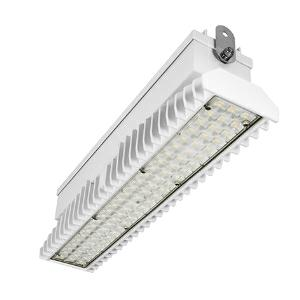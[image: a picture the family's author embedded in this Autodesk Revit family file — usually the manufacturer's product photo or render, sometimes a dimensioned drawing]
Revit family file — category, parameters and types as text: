
# Revit family: 3f_filippi_-_3f_lem_ho_ampio_3f_filippi_-_58953_a0811_-_3f_lem_1_ho_led_70_cr_ampio___vt_01d9
name_source: partatom
category: Lighting Fixtures
units: mm (PartAtom-declared; Revit-internal decimal feet)

## family parameters
Cut with Voids When Loaded = No
Host = Face
Light Source = No
Part Type = Normal
Room Calculation Point = No
Round Connector Dimension = Use Diameter
Shared = No

## types (1)
- 3F Filippi - 3F LEM HO Ampio (1 x LED, 10526 lm, 71 W, 4000 K)
    Apparent Load = 71 VA
    Approval mark = CE
    CIE Flux Codes = 60 92 99 100 100
    Color Rendering = 80
    Color Temperature = 4000 K
    Control Gear = Electronic ballast
    Default Elevation = 1800 mm
    Description = Industrial luminaire with high light output and high luminous efficiency designed with the most innovative technologies for environments with temperature up to 55°C.

ILLUMINOTECHNICAL
Luminous efficiency 100% (DLOR 99%, ULOR 1%).
Initial luminous flux of the luminaire 10526 lm.
Direct symmetric wide distribution: the illuminated area has a rectangular shape.
Installation Interdistance Transv.D = 1.58 x hu - Long.D = 1.45 x hu.
Tabular UGR (CIE 117 - 4H-8H; S=0.25H; 70/50/20): RUG 26.9 - 27.8.
Beam angle: 93° - 99°.
Luminous efficacy 148 lm/W.
Lifetime (L93/B10): 30000 h. (tq+25°C)
Lifetime (L90/B10): 50000 h. (tq+25°C)
Lifetime (L85/B10): 80000 h. (tq+25°C)
Lifetime (L80/B10): 100000 h. (tq+25°C)
Lifetime (L85/B10): 50000 h. (tq+55°C)
Sudden decreased luminous flux after 50000 hours: 0% (C0).
Photobiological safety in compliance with IEC/TR 62778: RG0 risk exempt, (IEC 62471).
In compliance with IEC/EN 62722-2-1 - IEC/EN 62717 standards.

SOURCE
Mid-Power linear LED module 70W/840.
Energy efficiency class (UE 2019/2020 - UE 2019/2015): C.
CIE 13.3 Colour rendering index: CRI >80 (R9 <50%).
IES TM-30 Fidelity Index: Rf = 84 Rg = 95.
CCT nominal colour temperature 4000 K.
Colour initial tolerance (MacAdam): SDCM 3.

MECHANICAL
Passive modular heatsinks in die-casted aluminium, painted in white colour.
To optimize the thermal management of the LED module, the heatsinks are oversized and provided with self-cleaning of cooling fins.
Wiring body in aluminium and galvanised steel anchored solidly to the sinks and thermally separated.
3F Lens lenses with high luminous efficiency, transparent methacrylate (PMMA), fixed to the LED modules.
Fixing brackets in stainless steel.
Luminaire with limited surface temperature. - D - (EN 60598-2-24)
Dimensions: 542x115 mm, height 154 mm. Weight 6.477 kg.
IP65 protection degree.
Mechanical strength to impacts IK06 (1 joule).
Glow-wire test resistance 650°C.

ELECTRICAL
Halogen Free electronic wiring 230V-50/60Hz, power factor 0.97, THD <25%, constant output current, class I, 1 driver.
Power of the luminaire 71 W.
ENEC - CE.
SAFE FLICKER: PstLM=<1 and SVM=<0.4 (IEC TR 61547-1 and IEC TR 63158), to ensure a more comfortable and safe light.
Luminaire compliant with EN 60598-2-22 for power supply from a centralised emergency system CPSS (Central Power Supply System), not incorporated in the luminaire - high risk areas excluded. The default power and flux are 100% in AC and 100% in DC.
Ambient temperature from -30°C to +55°C.
Temperature class T6 max 85°C.
Quick connection via M20 3P connector with 9-13 mm tightening range.
Power unit positioned on a separate compartment by the LED module to ensure optimum temperatures of cabling components, to be inspectable and maintainable.
Relative humidity UR: <85%.

INSTALLATION
Ceiling / Suspended / Wall.
All accessories dedicated to this product are available on the Catalog and on our website www.3F-Filippi.com.

ACCESSORIES
A0811 - VT transparent glass, tempered, not flammable, with sealing gasket.
One required for each light module. The pack contains 10 pieces.

APPLICATIONS
In commercial environments, exhibition and industrial areas, stores, open areas.
Environments in which it is necessary a total protection against falling fragments (eg environments with foodstuffs or machines with moving parts or with extreme temperature changes), use luminaires with polycarbonate lenses.

WARNING
Fixture not suitable for cold stores with an ambient temperature <0°C and/or relative humidity >85%.
Luminaire designed for disposal/recycling at end-of-life.
Replaceable (LED only) light source by a professional. Replaceable control gear by a professional.
    Height = 154 mm
    Lamp = 1 x LED
    Lamp Light Flux = 10526 lm
    Lamp Power = 71 W
    Lamp count = 1
    Length = 542 mm
    Lifetime = 50000 h
    Luminous efficacy = 148 lm/W
    Manufacturer = 3F Filippi
    ModVariant = No
    Model = 3F Filippi - 58953+A0811 - 3F LEM 1 HO LED 70 CR AMPIO + VT
    Mounting Place = Ceiling
    Mounting Type = Pendant
    Number of Poles = 1
    OnlyDefault = Yes
    Power Factor = 1
    Product Name = 3F Filippi - 3F LEM HO Ampio
    Product group = pendant luminaire
    ProductGroupID = 9
    Protection Class = Protection class I
    Protection Degree = IP 65
    RLX_Detail_Level = 1
    RLX_Emergency_Light_Flux = 0 lm
    RLX_Emergency_Type = 0
    RLX_Emergency_Type_DB = No
    RlxData = <blob elided: 94345 chars, md5=ea9f7cec>
    Socket = socket
    Standby Power = 0 W
    System Light Flux = 10526 lm
    System Power = 71 W
    Type Comments = Product without accessories
    Type Image = 3f_filippi_-_lem_1__a0811.jpg
    URL = http://relux.com
    VarID = ---
    Voltage = 0 V
    Weight = 0.00 kg
    Width = 115 mm

## geometry (parser evidence)
native form markers: Blend x4, Sweep x12
no freeform markers — native parametric forms only
